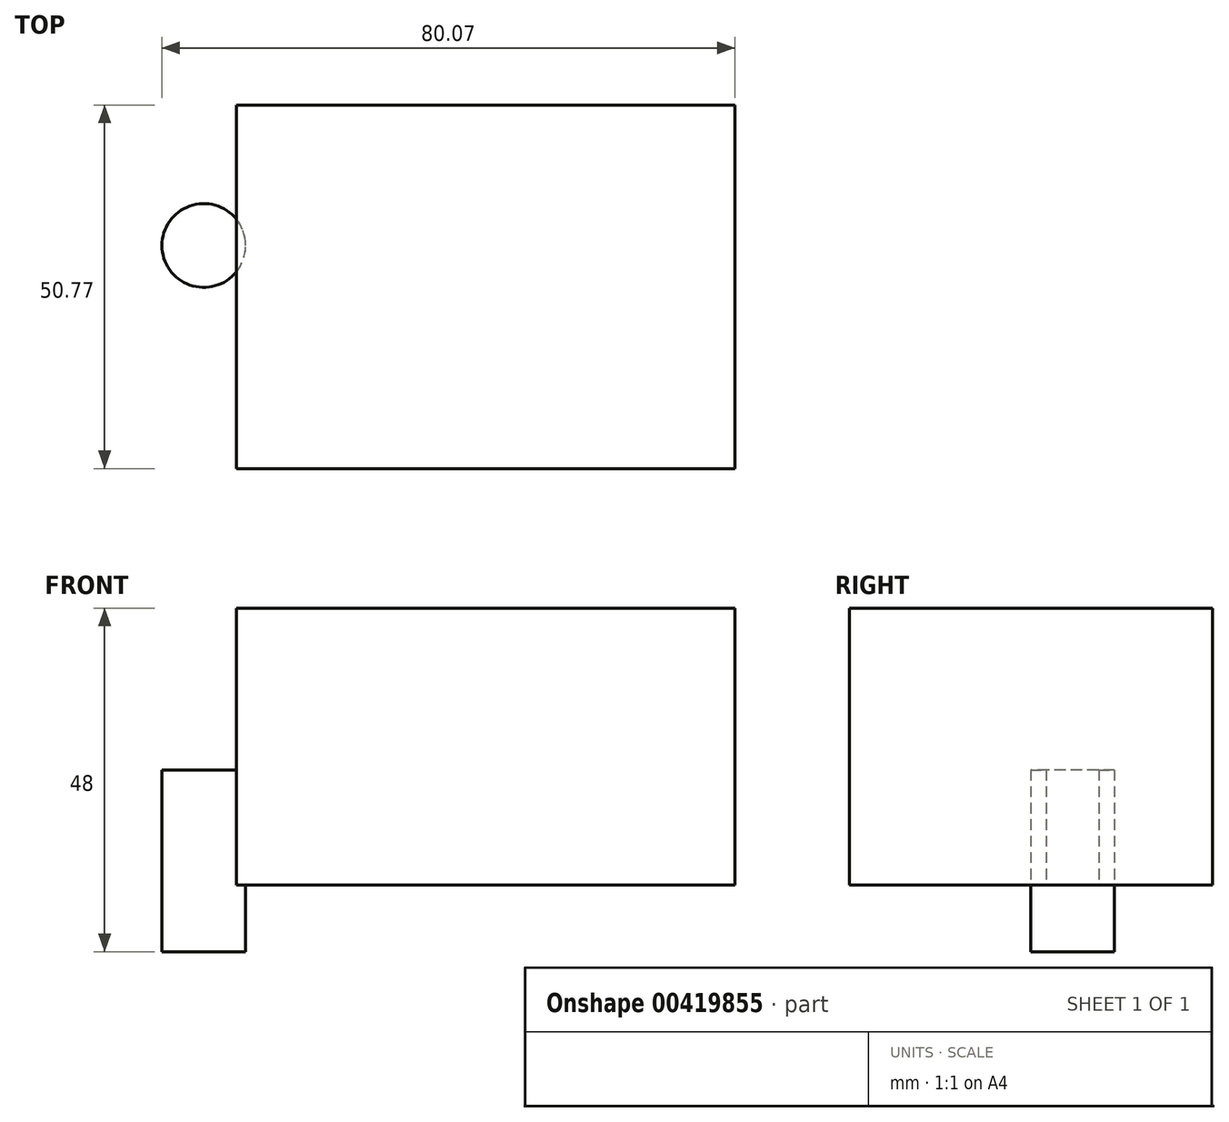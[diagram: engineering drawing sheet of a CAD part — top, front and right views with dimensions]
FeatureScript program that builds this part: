
annotation { "Feature Type Name" : "Feature", "Feature Type Description" : "" }
export const myFeature = defineFeature(function(context is Context, id is Id, definition is map)
    precondition{}
    {
        {
            var Q0;
            Q0=qCreatedBy(makeId("Front.planeOp"),FACE);
            var sketch = newSketch(context, id + "F0", { "sketchPlane" : qUnion([Q0])});
            skLineSegment(sketch, "E0.bottom", {"start": v(-36.4, 48) * mm, "end": v(33.26, 48) * mm});
            skLineSegment(sketch, "E0.top", {"start": v(-36.4, 9.32) * mm, "end": v(33.26, 9.32) * mm});
            skLineSegment(sketch, "E0.left", {"start": v(-36.4, 48) * mm, "end": v(-36.4, 9.32) * mm});
            skLineSegment(sketch, "E0.right", {"start": v(33.26, 48) * mm, "end": v(33.26, 9.32) * mm});
            skSolve(sketch);
        }
        {
            var Q0;
            Q0=makeQuery(id+"F0.imprint","IMPRINT",FACE,{"disambiguationData":[TD([[makeQuery(id+"F0.imprint","IMPRINT",EDGE,{"derivedFrom":sQuery(id+"F0.wireOp",EDGE,"E0.bottom")}),-1.0]])]});
            extrude(context, id + "F1", {"entities" : qUnion([Q0]), "depth" : 50.77 * mm});
        }
        {
            var Q0;
            Q0=qCreatedBy(makeId("Top.planeOp"),FACE);
            var sketch = newSketch(context, id + "F2", { "sketchPlane" : qUnion([Q0])});
            skCircle(sketch, "E1", {"center": v(-40.96, -19.6) * mm, "radius": 5.85 * mm});
            skSolve(sketch);
        }
        {
            var Q0;
            Q0 = qSketchRegion(id + "F2", true);
            extrude(context, id + "F3", {"entities" : qUnion([Q0]), "operationType" : NewBodyOperationType.ADD, "depth" : 25.4 * mm});
        }
    });
